# Revit family: console-hansgrohe-54210XXX-Xevolos E Console 1180_550 with cutout middle for countertop basin ground 500_480 and 600_480
name_source: partatom
category: Furniture
units: mm (PartAtom-declared; Revit-internal decimal feet)

## family parameters
Always vertical = Yes
Cut with Voids When Loaded = No
OmniClass Number = 23.40.00.00
OmniClass Title = Equipment and Furnishings
Room Calculation Point = No
Shared = Yes
Work Plane-Based = No

## types (6) — shared parameters
BASENUMBER = 54210
BIMOBJECT = Sanitary: Compound units
CATALOG = Hansgrohe
DESIGN = Germany
ETIM = EC011381 | Bathroom furniture set
IFC = Furnishing element
L = 1184
L1 = 300
LL = 592
MASTERFORMAT = 12 35 30.23 | Bathroom Casework
Manufacturer = Hansgrohe
NAME = Xevolos E Console 1180/550 with cutout middle for countertop basin ground 500/480 and 600/480
NBSYN = $BASENUMBER.-$ARTNR.-$SURFACE.-$LODLEVEL.
NN = Console with cutout for countertop basin ground
OBJECTTYPE = Object (single object)
OMNICLASS = 23-19 31 17 11 | Bathroom Units
PERMALINK = 54210XXX
PRODUCTFAMILY = Xevolos E
PRODUCTGROUP = console
REGIONSET = Worldwide
SPECIFICATION = https://pro.hansgrohe.com
UNICLASS2015 = Pr_40_20_76_94 | Vanity units
UNICLASS_2015_CODE = 40_30_78_05
UNIFORMATII = E2010 | Fixed Furnishings
UNSPSC = 56 | Furniture and Furnishings
WEIGHT = 4.4
etim7_EC011381 = EC011381

## per-type parameters (varying)
| type | ARTNR | IDNR | LODLEVEL | SURFACE |
| 54210-54210700-MATTE_WHITE-200 | 54210700 | 13 | 200 | MATTE_WHITE |
| 54210-54210700-MATTE_WHITE-400 | 54210700 | 13 | 400 | MATTE_WHITE |
| 54210-54210760-SLATE_MATT_GREY-200 | 54210760 | 14 | 200 | SLATE_MATT_GREY |
| 54210-54210760-SLATE_MATT_GREY-400 | 54210760 | 14 | 400 | SLATE_MATT_GREY |
| 54210-54210780-SAND_MATT_BEIGE-200 | 54210780 | 15 | 200 | SAND_MATT_BEIGE |
| 54210-54210780-SAND_MATT_BEIGE-400 | 54210780 | 15 | 400 | SAND_MATT_BEIGE |

note: column(s) folded — value = type name in every type: LINA, Model, NB

type visibility flags: 6 boolean params named "<type name>_RX0RY0RZ0TX0TY0TZ0_V" — each type sets only its own to Yes (folded from table)

## geometry (parser evidence)
native form markers: Sweep x31
no freeform markers — native parametric forms only
